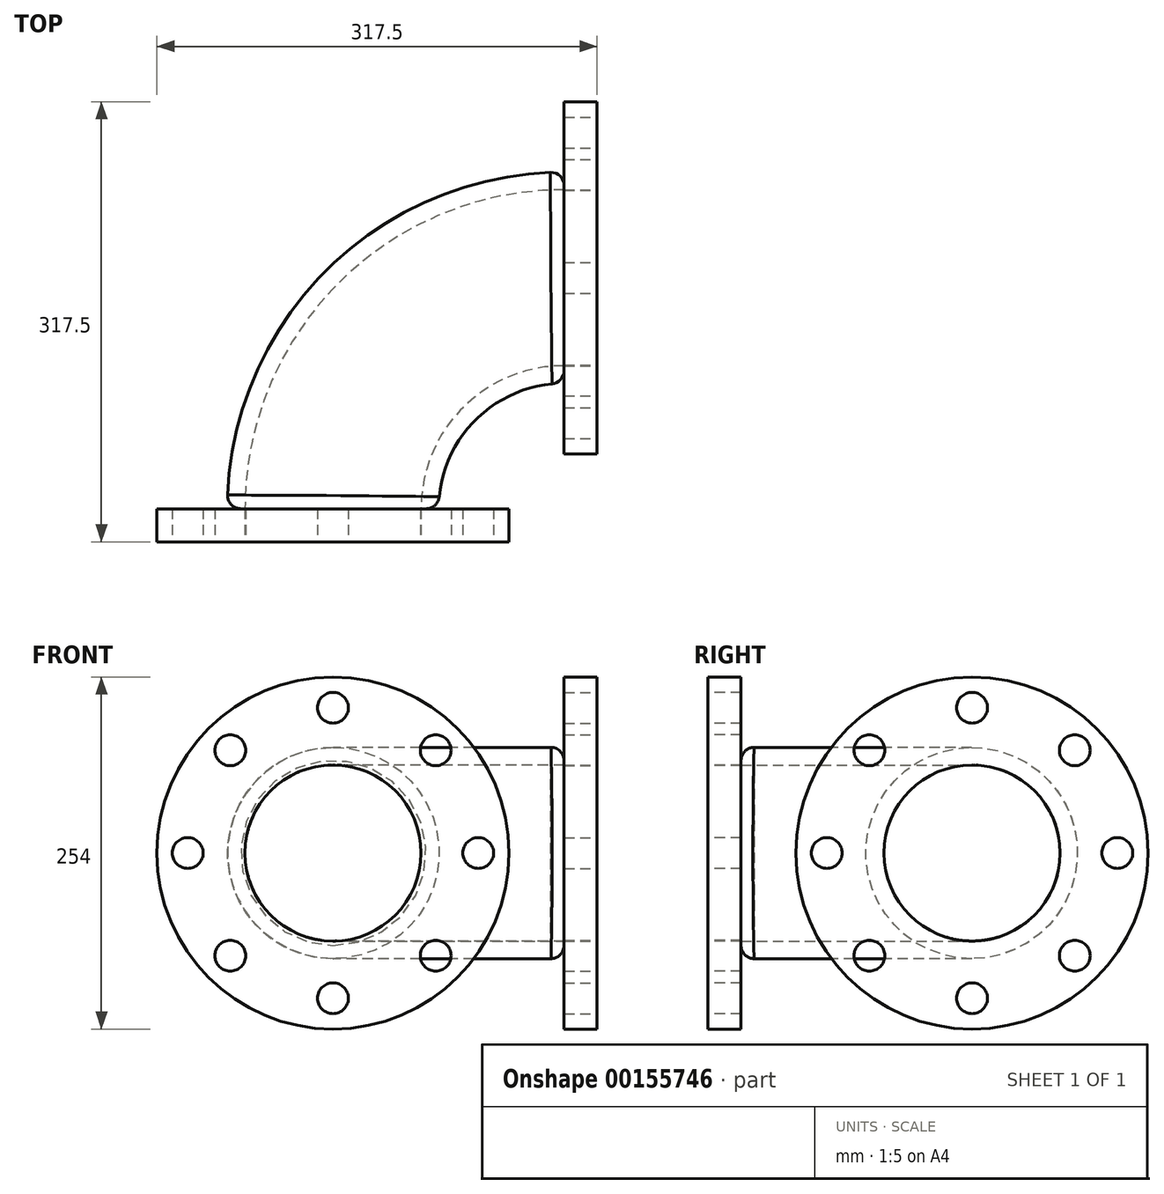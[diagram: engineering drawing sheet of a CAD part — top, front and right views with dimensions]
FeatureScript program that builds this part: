
annotation { "Feature Type Name" : "Feature", "Feature Type Description" : "" }
export const myFeature = defineFeature(function(context is Context, id is Id, definition is map)
    precondition{}
    {
        {
            var Q0;
            Q0=qCreatedBy(makeId("Top.planeOp"),FACE);
            var sketch = newSketch(context, id + "F0", { "sketchPlane" : qUnion([Q0])});
            skLineSegment(sketch, "E0", {"start": v(-190.5, 0) * mm, "end": v(-190.5, 23.81) * mm});
            skLineSegment(sketch, "E1", {"start": v(-23.81, 190.5) * mm, "end": v(0, 190.5) * mm});
            skPoint(sketch, "E2.visualSharp", {"position": v(-190.5, 190.5) * mm});
            skArc(sketch, "E2.filletArc", {"start": v(-23.81, 190.5) * mm, "mid": v(-141.68, 141.68) * mm, "end": v(-190.5, 23.81) * mm});
            skSolve(sketch);
        }
        {
            var Q0;
            Q0=qCreatedBy(makeId("Front.planeOp"),FACE);
            var sketch = newSketch(context, id + "F1", { "sketchPlane" : qUnion([Q0])});
            skCircle(sketch, "E3", {"center": v(-190.5, 0) * mm, "radius": 127 * mm});
            skCircle(sketch, "E4", {"center": v(-190.5, 0) * mm, "radius": 63.5 * mm});
            skCircle(sketch, "E5", {"center": v(-190.5, 0) * mm, "radius": 104.78 * mm, "construction": true});
            skCircle(sketch, "E6", {"center": v(-295.28, 0) * mm, "radius": 11.11 * mm});
            skCircle(sketch, "E7.1.0", {"center": v(-264.59, -74.09) * mm, "radius": 11.11 * mm});
            skCircle(sketch, "E7.2.0", {"center": v(-190.5, -104.78) * mm, "radius": 11.11 * mm});
            skCircle(sketch, "E7.3.0", {"center": v(-116.41, -74.09) * mm, "radius": 11.11 * mm});
            skCircle(sketch, "E7.4.0", {"center": v(-85.72, 0) * mm, "radius": 11.11 * mm});
            skCircle(sketch, "E7.5.0", {"center": v(-116.41, 74.09) * mm, "radius": 11.11 * mm});
            skCircle(sketch, "E7.6.0", {"center": v(-190.5, 104.78) * mm, "radius": 11.11 * mm});
            skCircle(sketch, "E7.7.0", {"center": v(-264.59, 74.09) * mm, "radius": 11.11 * mm});
            skSolve(sketch);
        }
        {
            var Q0;
            Q0=qCreatedBy(makeId("Right.planeOp"),FACE);
            var sketch = newSketch(context, id + "F2", { "sketchPlane" : qUnion([Q0])});
            skCircle(sketch, "E8", {"center": v(190.5, 0) * mm, "radius": 127 * mm});
            skCircle(sketch, "E9", {"center": v(190.5, 0) * mm, "radius": 63.5 * mm});
            skCircle(sketch, "E10", {"center": v(190.5, 0) * mm, "radius": 104.78 * mm, "construction": true});
            skCircle(sketch, "E11", {"center": v(85.72, 0) * mm, "radius": 11.11 * mm});
            skCircle(sketch, "E12.1.0", {"center": v(116.41, -74.09) * mm, "radius": 11.11 * mm});
            skCircle(sketch, "E12.2.0", {"center": v(190.5, -104.78) * mm, "radius": 11.11 * mm});
            skCircle(sketch, "E12.3.0", {"center": v(264.59, -74.09) * mm, "radius": 11.11 * mm});
            skCircle(sketch, "E12.4.0", {"center": v(295.28, 0) * mm, "radius": 11.11 * mm});
            skCircle(sketch, "E12.5.0", {"center": v(264.59, 74.09) * mm, "radius": 11.11 * mm});
            skCircle(sketch, "E12.6.0", {"center": v(190.5, 104.78) * mm, "radius": 11.11 * mm});
            skCircle(sketch, "E12.7.0", {"center": v(116.41, 74.09) * mm, "radius": 11.11 * mm});
            skSolve(sketch);
        }
        {
            var Q0;
            Q0=sQuery(id+"F0.wireOp",VERTEX,"E2.filletArc.end");
            var Q1;
            Q1=qCreatedBy(makeId("Front.planeOp"),FACE);
            cPlane(context, id + "F3", {"entities" : qUnion([Q0, Q1]), "cplaneType" : CPlaneType.PLANE_POINT, "offset" : 25.4 * mm, "width" : 152.4 * mm, "height" : 152.4 * mm});
        }
        {
            var Q0;
            Q0=qCreatedBy(id+"F3.planeOp",FACE);
            var sketch = newSketch(context, id + "F4", { "sketchPlane" : qUnion([Q0])});
            skCircle(sketch, "E13", {"center": v(-190.5, 0) * mm, "radius": 63.5 * mm});
            skCircle(sketch, "E14.0", {"center": v(-190.5, 0) * mm, "radius": 76.2 * mm});
            skSolve(sketch);
        }
        {
            var Q0;
            Q0=makeQuery(id+"F4.imprint","IMPRINT",FACE,{"disambiguationData":[TD([[makeQuery(id+"F4.imprint","IMPRINT",EDGE,{"derivedFrom":sQuery(id+"F4.wireOp",EDGE,"E13")}),-1.0]])]});
            var Q1;
            Q1=sQuery(id+"F4.wireOp",EDGE,"E13");
            var Q2;
            Q2=sQuery(id+"F4.wireOp",EDGE,"E14.0");
            var Q3;
            Q3=sQuery(id+"F0.wireOp",EDGE,"E2.filletArc");
            sweep(context, id + "F5", {"profiles" : qUnion([Q0]), "surfaceProfiles" : qUnion([Q1, Q2]), "path" : qUnion([Q3])});
        }
        {
            var Q0;
            Q0=makeQuery(id+"F1.imprint","IMPRINT",FACE,{"disambiguationData":[TD([[makeQuery(id+"F1.imprint","IMPRINT",EDGE,{"derivedFrom":sQuery(id+"F1.wireOp",EDGE,"E3")}),1.0]])]});
            var Q1;
            Q1=sQuery(id+"F1.wireOp",EDGE,"E4");
            var Q2;
            Q2=sQuery(id+"F1.wireOp",EDGE,"E3");
            extrude(context, id + "F6", {"entities" : qUnion([Q0]), "operationType" : NewBodyOperationType.ADD, "surfaceEntities" : qUnion([Q1, Q2]), "oppositeDirection" : true, "depth" : 23.8 * mm});
        }
        {
            var Q0;
            Q0=makeQuery(id+"F2.imprint","IMPRINT",FACE,{"disambiguationData":[TD([[makeQuery(id+"F2.imprint","IMPRINT",EDGE,{"derivedFrom":sQuery(id+"F2.wireOp",EDGE,"E8")}),1.0]])]});
            extrude(context, id + "F7", {"entities" : qUnion([Q0]), "operationType" : NewBodyOperationType.ADD, "oppositeDirection" : true, "depth" : 23.8 * mm});
        }
        {
            var Q0;
            Q0=makeQuery(id+"F5.opSweep","CAP_EDGE",EDGE,{"disambiguationData":[OSD([sQuery(id+"F0.wireOp",VERTEX,"E2.filletArc.start"),sQuery(id+"F4.wireOp",EDGE,"E14.0")])],"isStart":false});
            var Q1;
            Q1=makeQuery(id+"F5.opSweep","CAP_EDGE",EDGE,{"disambiguationData":[OSD([sQuery(id+"F0.wireOp",VERTEX,"E2.filletArc.end"),sQuery(id+"F4.wireOp",EDGE,"E14.0")])],"isStart":true});
            fillet(context, id + "F8", {"entities" : qUnion([Q0, Q1]), "radius" : 9.52 * mm, "tangentPropagation" : true, "allowEdgeOverflow" : false});
        }
    });
